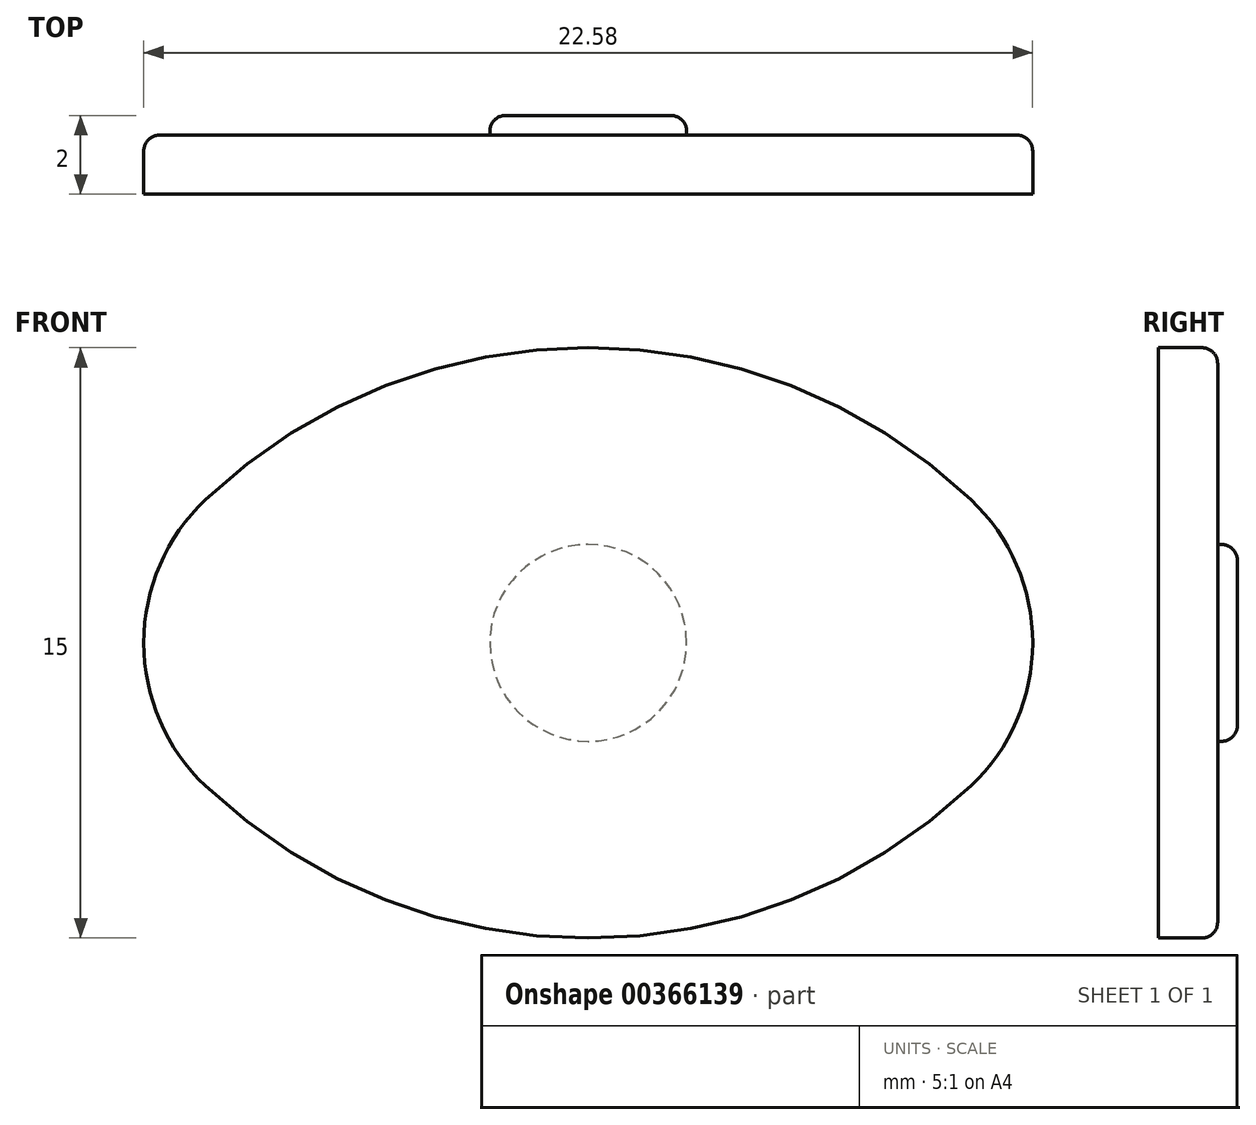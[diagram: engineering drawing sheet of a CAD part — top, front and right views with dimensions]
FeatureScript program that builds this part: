
annotation { "Feature Type Name" : "Feature", "Feature Type Description" : "" }
export const myFeature = defineFeature(function(context is Context, id is Id, definition is map)
    precondition{}
    {
        {
            var Q0;
            Q0=qCreatedBy(makeId("Front.planeOp"),FACE);
            var sketch = newSketch(context, id + "F0", { "sketchPlane" : qUnion([Q0])});
            skLineSegment(sketch, "E0.bottom", {"start": v(-12.5, 7.5) * mm, "end": v(12.5, 7.5) * mm, "construction": true});
            skLineSegment(sketch, "E0.top", {"start": v(-12.5, -7.5) * mm, "end": v(12.5, -7.5) * mm, "construction": true});
            skLineSegment(sketch, "E0.left", {"start": v(-12.5, 7.5) * mm, "end": v(-12.5, -7.5) * mm, "construction": true});
            skLineSegment(sketch, "E0.right", {"start": v(12.5, 7.5) * mm, "end": v(12.5, -7.5) * mm, "construction": true});
            skArc(sketch, "E1", {"start": v(12.5, 0) * mm, "mid": v(0, 7.5) * mm, "end": v(-12.5, 0) * mm});
            skArc(sketch, "E2", {"start": v(-12.5, 0) * mm, "mid": v(0, -7.5) * mm, "end": v(12.5, 0) * mm});
            skSolve(sketch);
        }
        {
            var Q0;
            Q0=makeQuery(id+"F0.imprint","IMPRINT",FACE,{"disambiguationData":[TD([[makeQuery(id+"F0.imprint","IMPRINT",EDGE,{"derivedFrom":sQuery(id+"F0.wireOp",EDGE,"E1")}),1.0]])]});
            var Q1;
            Q1=sQuery(id+"F0.wireOp",EDGE,"E0.right");
            var Q2;
            Q2=sQuery(id+"F0.wireOp",EDGE,"E0.left");
            var Q3;
            Q3=sQuery(id+"F0.wireOp",EDGE,"E0.bottom");
            var Q4;
            Q4=sQuery(id+"F0.wireOp",EDGE,"E0.top");
            extrude(context, id + "F1", {"entities" : qUnion([Q0]), "surfaceEntities" : qUnion([Q1, Q2, Q3, Q4]), "depth" : 1.5 * mm});
        }
        {
            var Q0;
            {var subQ0=sQuery(id+"F0.wireOp",EDGE,"E2");var subQ1=sQuery(id+"F0.wireOp",EDGE,"E1");Q0=makeQuery(id+"F1.opExtrude","SWEPT_EDGE",EDGE,{"disambiguationData":[OSD([subQ1,subQ0]),TDD([makeQuery(id+"F0.imprint","INTERSECT",VERTEX,{"disambiguationData":[OD(0.0)],"derivedFrom":[subQ1,subQ0]})])]});}
            var Q1;
            {var subQ0=sQuery(id+"F0.wireOp",EDGE,"E2");var subQ1=sQuery(id+"F0.wireOp",EDGE,"E1");Q1=makeQuery(id+"F1.opExtrude","SWEPT_EDGE",EDGE,{"disambiguationData":[OSD([subQ1,subQ0]),TDD([makeQuery(id+"F0.imprint","INTERSECT",VERTEX,{"disambiguationData":[OD(1.0)],"derivedFrom":[subQ1,subQ0]})])]});}
            fillet(context, id + "F2", {"entities" : qUnion([Q0, Q1]), "radius" : 5 * mm, "tangentPropagation" : true, "allowEdgeOverflow" : false});
        }
        {
            var Q0;
            Q0=makeQuery(id+"F1.opExtrude","CAP_FACE",FACE,{"disambiguationData":[OSD([sQuery(id+"F0.wireOp",EDGE,"E1"),sQuery(id+"F0.wireOp",EDGE,"E2")])],"isStart":true});
            var sketch = newSketch(context, id + "F3", { "sketchPlane" : qUnion([Q0])});
            skCircle(sketch, "E3", {"center": v(0, 0) * mm, "radius": 2.5 * mm});
            skSolve(sketch);
        }
        {
            var Q0;
            Q0 = qSketchRegion(id + "F3", true);
            extrude(context, id + "F4", {"entities" : qUnion([Q0]), "operationType" : NewBodyOperationType.ADD, "depth" : 0.5 * mm});
        }
        {
            var Q0;
            Q0=makeQuery(id+"F4.opExtrude","CAP_EDGE",EDGE,{"disambiguationData":[OSD([sQuery(id+"F3.wireOp",EDGE,"E3")])],"isStart":false});
            var Q1;
            Q1=makeQuery(id+"F1.opExtrude","CAP_EDGE",EDGE,{"disambiguationData":[OSD([sQuery(id+"F0.wireOp",EDGE,"E1")])],"isStart":true});
            var Q2;
            {var subQ0=sQuery(id+"F0.wireOp",EDGE,"E2");var subQ1=sQuery(id+"F0.wireOp",EDGE,"E1");Q2=makeQuery(id+"F2.opFillet","BLEND_EDGE",EDGE,{"blendedFrom":[makeQuery(id+"F1.opExtrude","SWEPT_EDGE",EDGE,{"disambiguationData":[OSD([subQ1,subQ0]),TDD([makeQuery(id+"F0.imprint","INTERSECT",VERTEX,{"disambiguationData":[OD(1.0)],"derivedFrom":[subQ1,subQ0]})])]}),makeQuery(id+"F1.opExtrude","CAP_FACE",FACE,{"disambiguationData":[OSD([subQ1,subQ0])],"isStart":true})],"blendedInto":[makeQuery(id+"F1.opExtrude","CAP_FACE",FACE,{"disambiguationData":[OSD([subQ1,subQ0])],"isStart":true})]});}
            fillet(context, id + "F5", {"entities" : qUnion([Q0, Q1, Q2]), "radius" : 0.4 * mm, "tangentPropagation" : true, "allowEdgeOverflow" : false});
        }
    });
